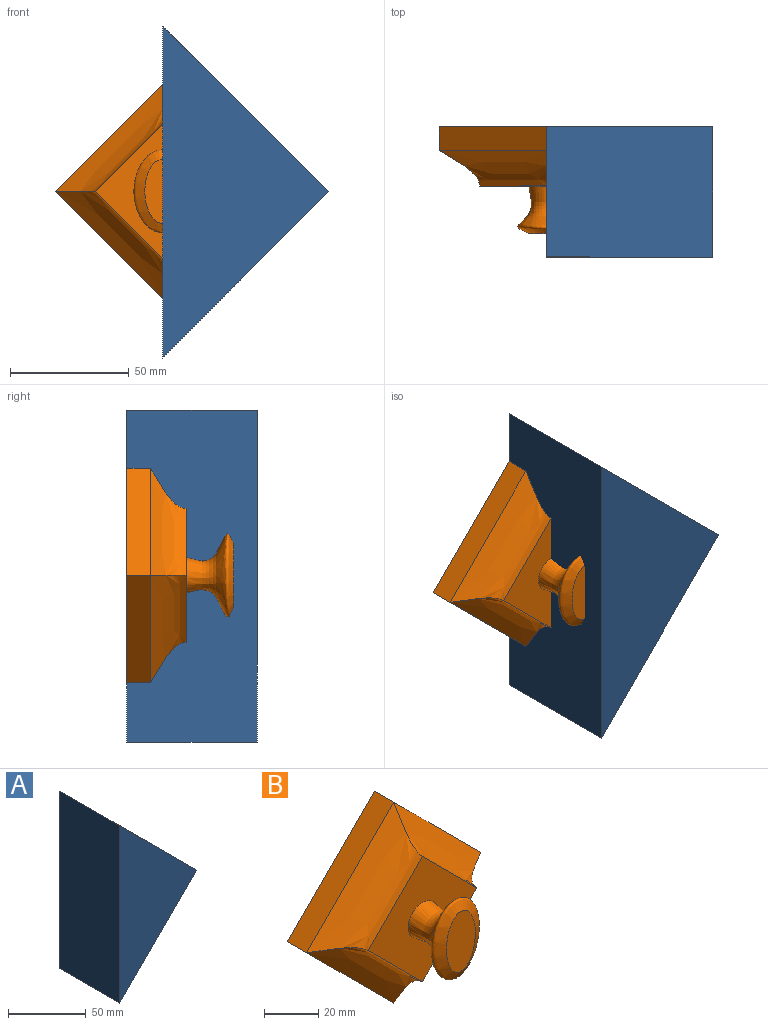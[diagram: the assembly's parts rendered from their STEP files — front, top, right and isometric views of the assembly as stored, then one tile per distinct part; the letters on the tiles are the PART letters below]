
ASSEMBLY  parts=2 mates=1
PART A: 5 faces, bbox 70x55x140 mm
  f0: plane 140x55mm, normal (-1,0,0), area 7700mm2, adj f1,f2,f3,f4
  f1: plane 70x70mm, normal (0.71,0,-0.71), area 5444.7mm2, adj f0,f2,f3,f4
  f2: plane 70x70mm, normal (0.71,0,0.71), area 5444.7mm2, adj f0,f1,f3,f4
  f3: plane 140x70mm, normal (0,-1,0), area 4900mm2, adj f0,f1,f2
  f4: plane 140x70mm, normal (0,1,0), area 4900mm2, adj f0,f1,f2
PART B: 12 faces, bbox 90.5x45x90.5 mm
  f0: plane 27.02x15.01mm, normal (0,-1,0), area 318.1mm2, adj f1
  f1: bspline ~41.82x29.83mm, area 1581.8mm2, adj f0,f2
  f2: plane 56.57x56.57mm, normal (0,-1,0), area 1423.4mm2, adj f1,f3,f4,f5,f6
  f3: bspline ~45.26x45.26mm, area 987.6mm2, adj f2,f4,f6,f10
  f4: bspline ~45.26x45.26mm, area 987.6mm2, adj f2,f3,f5,f9
  f5: bspline ~45.26x45.26mm, area 987.6mm2, adj f2,f4,f6,f8
  f6: bspline ~45.26x45.26mm, area 987.6mm2, adj f2,f3,f5,f7
  f7: plane 45.26x45.26mm, normal (-0.71,0,0.71), area 640mm2, adj f6,f8,f10,f11
  f8: plane 45.26x45.26mm, normal (0.71,0,0.71), area 640mm2, adj f5,f7,f9,f11
  f9: plane 45.26x45.26mm, normal (0.71,0,-0.71), area 640mm2, adj f4,f8,f10,f11
  f10: plane 45.26x45.26mm, normal (-0.71,0,-0.71), area 640mm2, adj f3,f7,f9,f11
  f11: plane 90.51x90.51mm, normal (0,1,0), area 4096mm2, adj f7,f8,f9,f10
PLACE A t=(-34.48,42.02,-48.95)mm
PLACE B t=(-34.48,17.02,-48.7)mm
MATE planar B.f11 <-> A.f4  axis (0,1,0) through (-34.48,42.02,-48.7)mm
